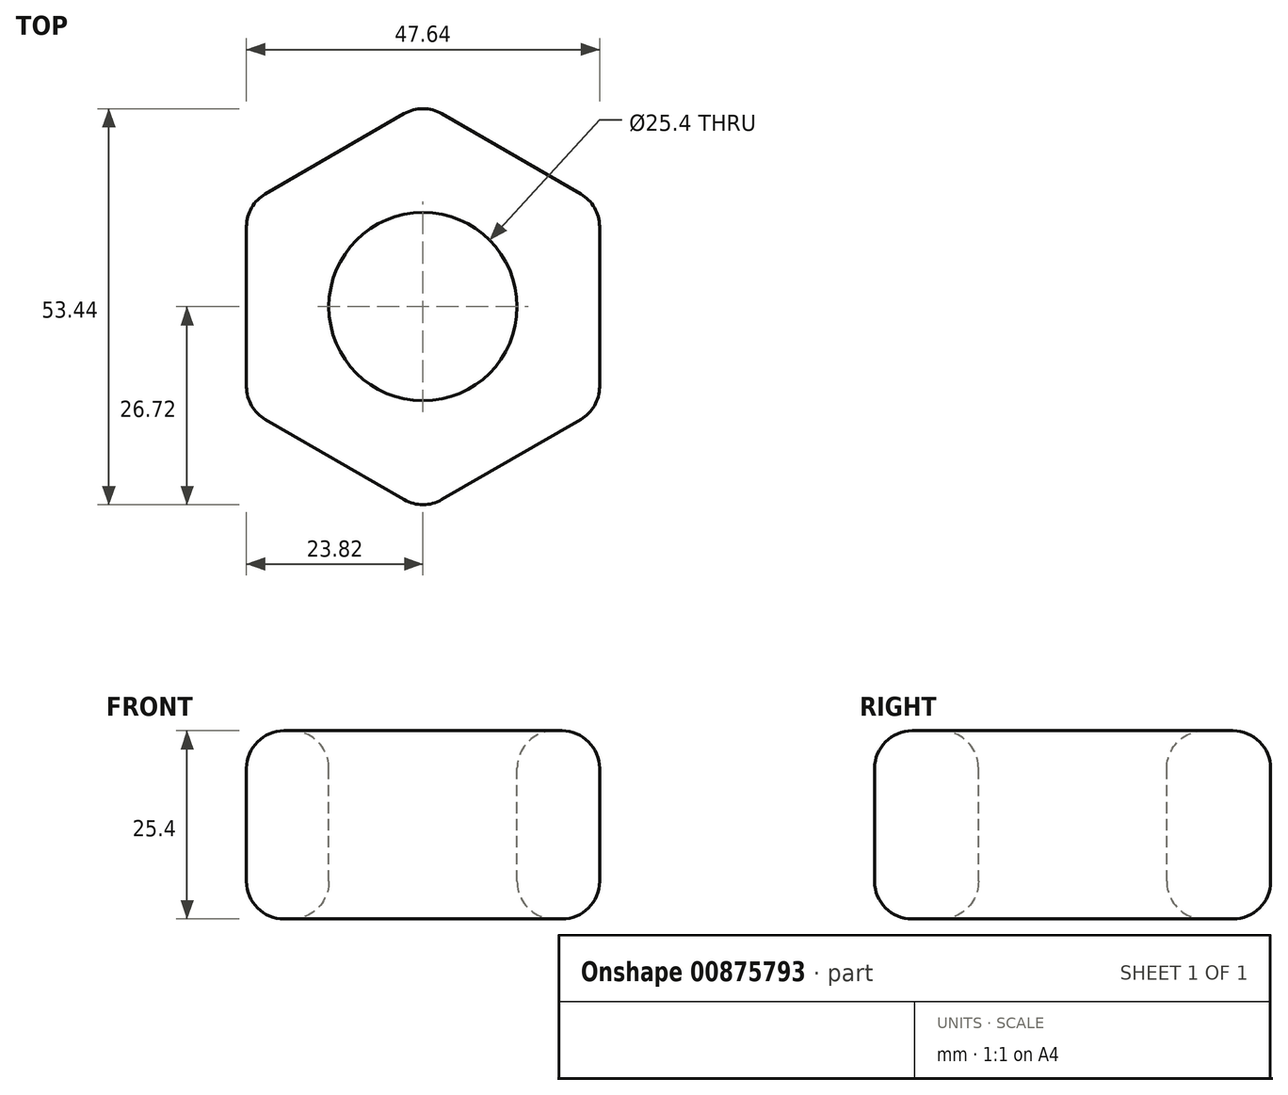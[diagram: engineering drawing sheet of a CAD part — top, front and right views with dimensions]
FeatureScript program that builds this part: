
annotation { "Feature Type Name" : "Feature", "Feature Type Description" : "" }
export const myFeature = defineFeature(function(context is Context, id is Id, definition is map)
    precondition{}
    {
        {
            var Q0;
            Q0=qCreatedBy(makeId("Top.planeOp"),FACE);
            var sketch = newSketch(context, id + "F0", { "sketchPlane" : qUnion([Q0])});
            skLineSegment(sketch, "E0", {"start": v(23.82, 13.75) * mm, "end": v(23.82, -13.75) * mm});
            skLineSegment(sketch, "E1", {"start": v(23.82, -13.75) * mm, "end": v(0, -27.5) * mm});
            skLineSegment(sketch, "E2", {"start": v(23.82, 13.75) * mm, "end": v(0, 27.5) * mm});
            skLineSegment(sketch, "E3", {"start": v(23.82, 0) * mm, "end": v(0, 0) * mm, "construction": true});
            skLineSegment(sketch, "E4.MirrorCS", {"start": v(-23.82, 13.75) * mm, "end": v(0, 27.5) * mm});
            skLineSegment(sketch, "E5.MirrorCS", {"start": v(-23.82, 13.75) * mm, "end": v(-23.82, -13.75) * mm});
            skLineSegment(sketch, "E6.MirrorCS", {"start": v(-23.82, -13.75) * mm, "end": v(0, -27.5) * mm});
            skSolve(sketch);
        }
        {
            var Q0;
            Q0 = qSketchRegion(id + "F0", true);
            extrude(context, id + "F1", {"entities" : qUnion([Q0]), "depth" : 25.4 * mm, "offsetDistance" : 25.4 * mm});
        }
        {
            var Q0;
            Q0=makeQuery(id+"F1.opExtrude","SWEPT_EDGE",EDGE,{"disambiguationData":[OSD([sQuery(id+"F0.wireOp",EDGE,"E0"),sQuery(id+"F0.wireOp",EDGE,"E2")])]});
            var Q1;
            Q1=makeQuery(id+"F1.opExtrude","SWEPT_EDGE",EDGE,{"disambiguationData":[OSD([sQuery(id+"F0.wireOp",EDGE,"E2"),sQuery(id+"F0.wireOp",EDGE,"E4.MirrorCS")])]});
            var Q2;
            Q2=makeQuery(id+"F1.opExtrude","SWEPT_EDGE",EDGE,{"disambiguationData":[OSD([sQuery(id+"F0.wireOp",EDGE,"E0"),sQuery(id+"F0.wireOp",EDGE,"E1")])]});
            var Q3;
            Q3=makeQuery(id+"F1.opExtrude","SWEPT_EDGE",EDGE,{"disambiguationData":[OSD([sQuery(id+"F0.wireOp",EDGE,"E1"),sQuery(id+"F0.wireOp",EDGE,"E6.MirrorCS")])]});
            var Q4;
            Q4=makeQuery(id+"F1.opExtrude","SWEPT_EDGE",EDGE,{"disambiguationData":[OSD([sQuery(id+"F0.wireOp",EDGE,"E5.MirrorCS"),sQuery(id+"F0.wireOp",EDGE,"E6.MirrorCS")])]});
            var Q5;
            Q5=makeQuery(id+"F1.opExtrude","SWEPT_EDGE",EDGE,{"disambiguationData":[OSD([sQuery(id+"F0.wireOp",EDGE,"E4.MirrorCS"),sQuery(id+"F0.wireOp",EDGE,"E5.MirrorCS")])]});
            fillet(context, id + "F2", {"entities" : qUnion([Q0, Q1, Q2, Q3, Q4, Q5]), "radius" : 5.08 * mm, "tangentPropagation" : true, "allowEdgeOverflow" : false});
        }
        {
            var Q0;
            Q0=makeQuery(id+"F1.opExtrude","CAP_FACE",FACE,{"disambiguationData":[OSD([sQuery(id+"F0.wireOp",EDGE,"E0"),sQuery(id+"F0.wireOp",EDGE,"E1"),sQuery(id+"F0.wireOp",EDGE,"E2"),sQuery(id+"F0.wireOp",EDGE,"E4.MirrorCS"),sQuery(id+"F0.wireOp",EDGE,"E5.MirrorCS"),sQuery(id+"F0.wireOp",EDGE,"E6.MirrorCS")])],"isStart":false});
            var Q1;
            Q1=makeQuery(id+"F1.opExtrude","CAP_FACE",FACE,{"disambiguationData":[OSD([sQuery(id+"F0.wireOp",EDGE,"E0"),sQuery(id+"F0.wireOp",EDGE,"E1"),sQuery(id+"F0.wireOp",EDGE,"E2"),sQuery(id+"F0.wireOp",EDGE,"E4.MirrorCS"),sQuery(id+"F0.wireOp",EDGE,"E5.MirrorCS"),sQuery(id+"F0.wireOp",EDGE,"E6.MirrorCS")])],"isStart":true});
            fillet(context, id + "F3", {"entities" : qUnion([Q0, Q1]), "radius" : 5.08 * mm, "tangentPropagation" : true, "allowEdgeOverflow" : false});
        }
        {
            var Q0;
            Q0=makeQuery(id+"F1.opExtrude","CAP_FACE",FACE,{"disambiguationData":[OSD([sQuery(id+"F0.wireOp",EDGE,"E0"),sQuery(id+"F0.wireOp",EDGE,"E1"),sQuery(id+"F0.wireOp",EDGE,"E2"),sQuery(id+"F0.wireOp",EDGE,"E4.MirrorCS"),sQuery(id+"F0.wireOp",EDGE,"E5.MirrorCS"),sQuery(id+"F0.wireOp",EDGE,"E6.MirrorCS")])],"isStart":false});
            var sketch = newSketch(context, id + "F4", { "sketchPlane" : qUnion([Q0])});
            skCircle(sketch, "E7", {"center": v(0, 0) * mm, "radius": 12.7 * mm});
            skSolve(sketch);
        }
        {
            var Q0;
            Q0 = qSketchRegion(id + "F4", true);
            extrude(context, id + "F5", {"entities" : qUnion([Q0]), "operationType" : NewBodyOperationType.REMOVE, "endBound" : BoundingType.THROUGH_ALL, "oppositeDirection" : true, "depth" : 25.4 * mm, "offsetDistance" : 25.4 * mm});
        }
        {
            var Q0;
            Q0=makeQuery(id+"F5.boolean.opBoolean","COPY",FACE,{"derivedFrom":makeQuery(id+"F5.opExtrude","SWEPT_FACE",FACE,{"disambiguationData":[OSD([sQuery(id+"F4.wireOp",EDGE,"E7")])]})});
            fillet(context, id + "F6", {"entities" : qUnion([Q0]), "radius" : 5.08 * mm, "tangentPropagation" : true, "allowEdgeOverflow" : false});
        }
    });
